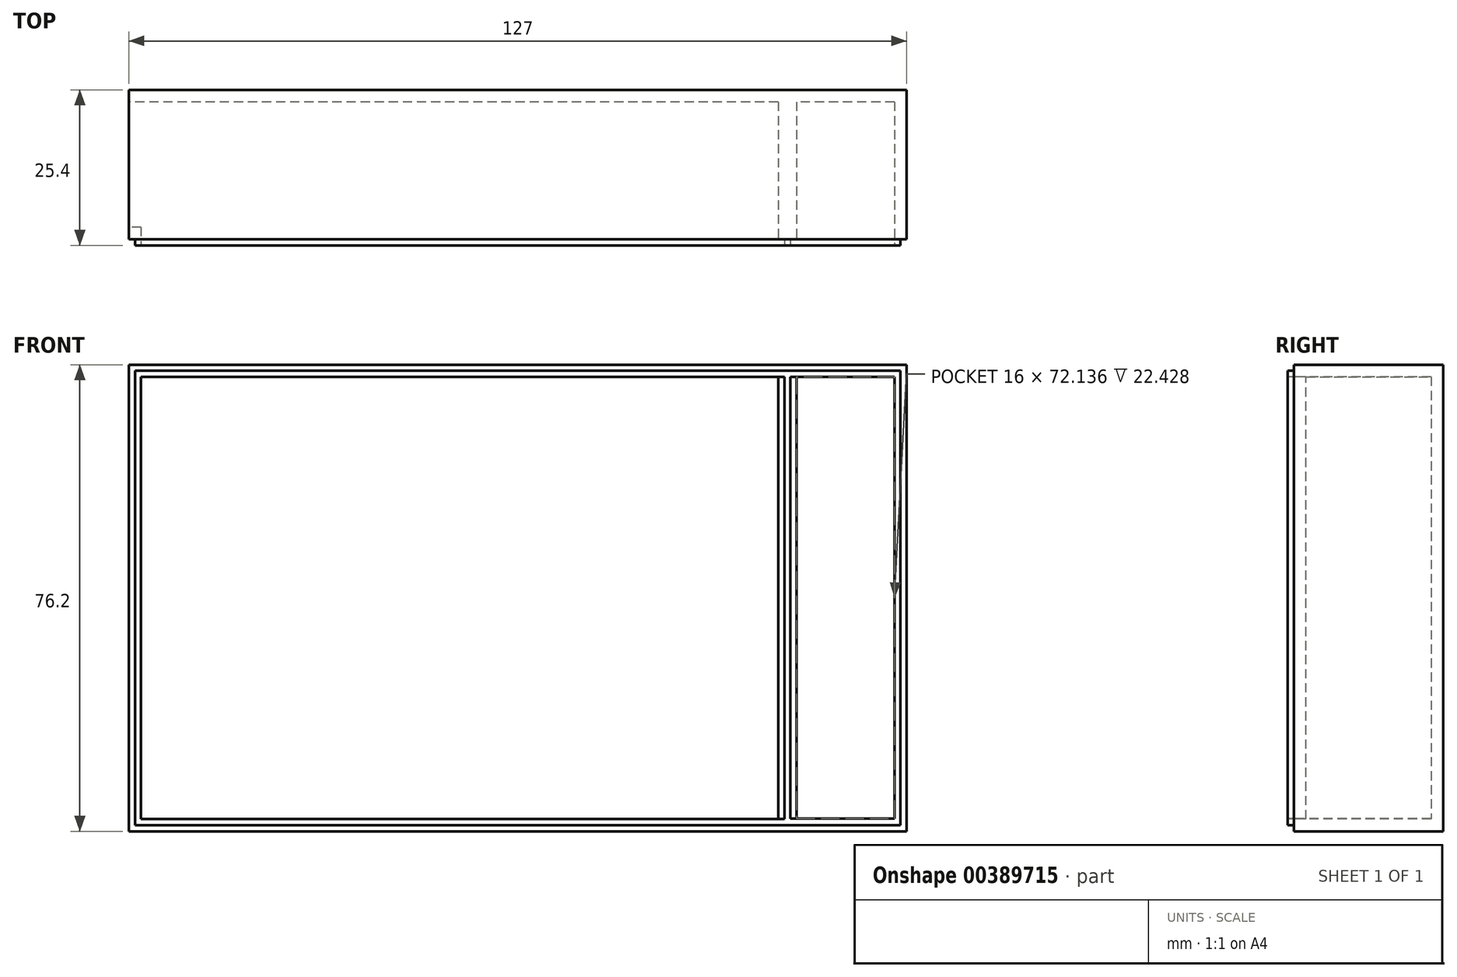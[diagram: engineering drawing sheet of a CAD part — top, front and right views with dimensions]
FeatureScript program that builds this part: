
annotation { "Feature Type Name" : "Feature", "Feature Type Description" : "" }
export const myFeature = defineFeature(function(context is Context, id is Id, definition is map)
    precondition{}
    {
        {
            var Q0;
            Q0=qCreatedBy(makeId("Front.planeOp"),FACE);
            var sketch = newSketch(context, id + "F0", { "sketchPlane" : qUnion([Q0])});
            skLineSegment(sketch, "E0.bottom", {"start": v(-63.5, 38.1) * mm, "end": v(63.5, 38.1) * mm});
            skLineSegment(sketch, "E0.top", {"start": v(-63.5, -38.1) * mm, "end": v(63.5, -38.1) * mm});
            skLineSegment(sketch, "E0.left", {"start": v(-63.5, 38.1) * mm, "end": v(-63.5, -38.1) * mm});
            skLineSegment(sketch, "E0.right", {"start": v(63.5, 38.1) * mm, "end": v(63.5, -38.1) * mm});
            skPoint(sketch, "E0.middle", {"position": v(0, 0) * mm});
            skSolve(sketch);
        }
        {
            var Q0;
            Q0=makeQuery(id+"F0.imprint","IMPRINT",FACE,{"disambiguationData":[TD([[makeQuery(id+"F0.imprint","IMPRINT",EDGE,{"derivedFrom":sQuery(id+"F0.wireOp",EDGE,"E0.bottom")}),-1.0]])]});
            extrude(context, id + "F1", {"entities" : qUnion([Q0]), "depth" : 25.4 * mm});
        }
        {
            var Q0;
            Q0=makeQuery(id+"F1.opExtrude","CAP_FACE",FACE,{"disambiguationData":[OSD([sQuery(id+"F0.wireOp",EDGE,"E0.bottom"),sQuery(id+"F0.wireOp",EDGE,"E0.top"),sQuery(id+"F0.wireOp",EDGE,"E0.left"),sQuery(id+"F0.wireOp",EDGE,"E0.right")])],"isStart":false});
            var sketch = newSketch(context, id + "F2", { "sketchPlane" : qUnion([Q0])});
            skLineSegment(sketch, "E1", {"start": v(45.52, 36.12) * mm, "end": v(45.52, -36.02) * mm});
            skLineSegment(sketch, "E2", {"start": v(45.52, -36.02) * mm, "end": v(61.52, -36.02) * mm});
            skLineSegment(sketch, "E3", {"start": v(61.52, -36.02) * mm, "end": v(61.52, 36.12) * mm});
            skLineSegment(sketch, "E4", {"start": v(61.52, 36.12) * mm, "end": v(45.52, 36.12) * mm});
            skSolve(sketch);
        }
        {
            var Q0;
            Q0=makeQuery(id+"F2.imprint","IMPRINT",FACE,{"disambiguationData":[TD([[makeQuery(id+"F2.imprint","IMPRINT",EDGE,{"derivedFrom":sQuery(id+"F2.wireOp",EDGE,"E1")}),1.0]])]});
            extrude(context, id + "F3", {"entities" : qUnion([Q0]), "operationType" : NewBodyOperationType.REMOVE, "oppositeDirection" : true, "depth" : 23.42 * mm});
        }
        {
            var Q0;
            Q0=makeQuery(id+"F1.opExtrude","CAP_FACE",FACE,{"disambiguationData":[OSD([sQuery(id+"F0.wireOp",EDGE,"E0.bottom"),sQuery(id+"F0.wireOp",EDGE,"E0.top"),sQuery(id+"F0.wireOp",EDGE,"E0.left"),sQuery(id+"F0.wireOp",EDGE,"E0.right")])],"isStart":false});
            var sketch = newSketch(context, id + "F4", { "sketchPlane" : qUnion([Q0])});
            skLineSegment(sketch, "E5.bottom", {"start": v(45.52, 36.12) * mm, "end": v(44.53, 36.12) * mm});
            skLineSegment(sketch, "E5.top", {"start": v(45.52, -36.02) * mm, "end": v(44.53, -36.02) * mm});
            skLineSegment(sketch, "E5.left", {"start": v(45.52, 36.12) * mm, "end": v(45.52, -36.02) * mm});
            skLineSegment(sketch, "E5.right", {"start": v(44.53, 36.12) * mm, "end": v(44.53, -36.02) * mm});
            skSolve(sketch);
        }
        {
            var Q0;
            Q0=makeQuery(id+"F4.imprint","IMPRINT",FACE,{"disambiguationData":[TD([[makeQuery(id+"F4.imprint","IMPRINT",EDGE,{"derivedFrom":sQuery(id+"F4.wireOp",EDGE,"E5.bottom")}),1.0]])]});
            extrude(context, id + "F5", {"entities" : qUnion([Q0]), "operationType" : NewBodyOperationType.REMOVE, "oppositeDirection" : true, "depth" : 1 * mm});
        }
        {
            var Q0;
            Q0=makeQuery(id+"F1.opExtrude","CAP_FACE",FACE,{"disambiguationData":[OSD([sQuery(id+"F0.wireOp",EDGE,"E0.bottom"),sQuery(id+"F0.wireOp",EDGE,"E0.top"),sQuery(id+"F0.wireOp",EDGE,"E0.left"),sQuery(id+"F0.wireOp",EDGE,"E0.right")])],"isStart":false});
            var sketch = newSketch(context, id + "F6", { "sketchPlane" : qUnion([Q0])});
            skLineSegment(sketch, "E6.bottom", {"start": v(-63.5, 38.1) * mm, "end": v(63.5, 38.1) * mm});
            skLineSegment(sketch, "E6.top", {"start": v(-63.5, 37.1) * mm, "end": v(63.5, 37.1) * mm});
            skLineSegment(sketch, "E6.left", {"start": v(-63.5, 38.1) * mm, "end": v(-63.5, 37.1) * mm});
            skLineSegment(sketch, "E6.right", {"start": v(63.5, 38.1) * mm, "end": v(63.5, 37.1) * mm});
            skSolve(sketch);
        }
        {
            var Q0;
            Q0=makeQuery(id+"F6.imprint","IMPRINT",FACE,{"disambiguationData":[TD([[makeQuery(id+"F6.imprint","IMPRINT",EDGE,{"derivedFrom":sQuery(id+"F6.wireOp",EDGE,"E6.bottom")}),-1.0]])]});
            extrude(context, id + "F7", {"entities" : qUnion([Q0]), "operationType" : NewBodyOperationType.REMOVE, "oppositeDirection" : true, "depth" : 1 * mm});
        }
        {
            var Q0;
            Q0=makeQuery(id+"F1.opExtrude","CAP_FACE",FACE,{"disambiguationData":[OSD([sQuery(id+"F0.wireOp",EDGE,"E0.bottom"),sQuery(id+"F0.wireOp",EDGE,"E0.top"),sQuery(id+"F0.wireOp",EDGE,"E0.left"),sQuery(id+"F0.wireOp",EDGE,"E0.right")])],"isStart":false});
            var sketch = newSketch(context, id + "F8", { "sketchPlane" : qUnion([Q0])});
            skLineSegment(sketch, "E7.bottom", {"start": v(63.5, 37.1) * mm, "end": v(62.5, 37.1) * mm});
            skLineSegment(sketch, "E7.top", {"start": v(63.5, -38.1) * mm, "end": v(62.5, -38.1) * mm});
            skLineSegment(sketch, "E7.left", {"start": v(63.5, 37.1) * mm, "end": v(63.5, -38.1) * mm});
            skLineSegment(sketch, "E7.right", {"start": v(62.5, 37.1) * mm, "end": v(62.5, -38.1) * mm});
            skSolve(sketch);
        }
        {
            var Q0;
            Q0=makeQuery(id+"F8.imprint","IMPRINT",FACE,{"disambiguationData":[TD([[makeQuery(id+"F8.imprint","IMPRINT",EDGE,{"derivedFrom":sQuery(id+"F8.wireOp",EDGE,"E7.bottom")}),-1.0]])]});
            extrude(context, id + "F9", {"entities" : qUnion([Q0]), "operationType" : NewBodyOperationType.REMOVE, "oppositeDirection" : true, "depth" : 1 * mm});
        }
        {
            var Q0;
            Q0=makeQuery(id+"F1.opExtrude","CAP_FACE",FACE,{"disambiguationData":[OSD([sQuery(id+"F0.wireOp",EDGE,"E0.bottom"),sQuery(id+"F0.wireOp",EDGE,"E0.top"),sQuery(id+"F0.wireOp",EDGE,"E0.left"),sQuery(id+"F0.wireOp",EDGE,"E0.right")])],"isStart":false});
            var sketch = newSketch(context, id + "F10", { "sketchPlane" : qUnion([Q0])});
            skLineSegment(sketch, "E8.bottom", {"start": v(-63.5, 37.1) * mm, "end": v(-62.5, 37.1) * mm});
            skLineSegment(sketch, "E8.top", {"start": v(-63.5, -38.1) * mm, "end": v(-62.5, -38.1) * mm});
            skLineSegment(sketch, "E8.left", {"start": v(-63.5, 37.1) * mm, "end": v(-63.5, -38.1) * mm});
            skLineSegment(sketch, "E8.right", {"start": v(-62.5, 37.1) * mm, "end": v(-62.5, -38.1) * mm});
            skSolve(sketch);
        }
        {
            var Q0;
            Q0=makeQuery(id+"F10.imprint","IMPRINT",FACE,{"disambiguationData":[TD([[makeQuery(id+"F10.imprint","IMPRINT",EDGE,{"derivedFrom":sQuery(id+"F10.wireOp",EDGE,"E8.bottom")}),-1.0]])]});
            extrude(context, id + "F11", {"entities" : qUnion([Q0]), "operationType" : NewBodyOperationType.REMOVE, "oppositeDirection" : true, "depth" : 1 * mm});
        }
        {
            var Q0;
            Q0=makeQuery(id+"F1.opExtrude","CAP_FACE",FACE,{"disambiguationData":[OSD([sQuery(id+"F0.wireOp",EDGE,"E0.bottom"),sQuery(id+"F0.wireOp",EDGE,"E0.top"),sQuery(id+"F0.wireOp",EDGE,"E0.left"),sQuery(id+"F0.wireOp",EDGE,"E0.right")])],"isStart":false});
            var sketch = newSketch(context, id + "F12", { "sketchPlane" : qUnion([Q0])});
            skLineSegment(sketch, "E9.bottom", {"start": v(-62.5, -38.1) * mm, "end": v(62.5, -38.1) * mm});
            skLineSegment(sketch, "E9.top", {"start": v(-62.5, -37.1) * mm, "end": v(62.5, -37.1) * mm});
            skLineSegment(sketch, "E9.left", {"start": v(-62.5, -38.1) * mm, "end": v(-62.5, -37.1) * mm});
            skLineSegment(sketch, "E9.right", {"start": v(62.5, -38.1) * mm, "end": v(62.5, -37.1) * mm});
            skSolve(sketch);
        }
        {
            var Q0;
            Q0=makeQuery(id+"F12.imprint","IMPRINT",FACE,{"disambiguationData":[TD([[makeQuery(id+"F12.imprint","IMPRINT",EDGE,{"derivedFrom":sQuery(id+"F12.wireOp",EDGE,"E9.bottom")}),1.0]])]});
            extrude(context, id + "F13", {"entities" : qUnion([Q0]), "operationType" : NewBodyOperationType.REMOVE, "oppositeDirection" : true, "depth" : 1 * mm});
        }
        {
            var Q0;
            Q0=makeQuery(id+"F1.opExtrude","CAP_FACE",FACE,{"disambiguationData":[OSD([sQuery(id+"F0.wireOp",EDGE,"E0.bottom"),sQuery(id+"F0.wireOp",EDGE,"E0.top"),sQuery(id+"F0.wireOp",EDGE,"E0.left"),sQuery(id+"F0.wireOp",EDGE,"E0.right")])],"isStart":false});
            var sketch = newSketch(context, id + "F14", { "sketchPlane" : qUnion([Q0])});
            skLineSegment(sketch, "E10", {"start": v(-61.52, 36.12) * mm, "end": v(-61.52, -36.12) * mm});
            skLineSegment(sketch, "E11", {"start": v(-61.52, -36.12) * mm, "end": v(42.55, -36.12) * mm});
            skLineSegment(sketch, "E12", {"start": v(42.55, -36.12) * mm, "end": v(42.55, 36.12) * mm});
            skLineSegment(sketch, "E13", {"start": v(42.55, 36.12) * mm, "end": v(-61.52, 36.12) * mm});
            skSolve(sketch);
        }
        {
            var Q0;
            Q0=makeQuery(id+"F14.imprint","IMPRINT",FACE,{"disambiguationData":[TD([[makeQuery(id+"F14.imprint","IMPRINT",EDGE,{"derivedFrom":sQuery(id+"F14.wireOp",EDGE,"E10")}),1.0]])]});
            extrude(context, id + "F15", {"entities" : qUnion([Q0]), "operationType" : NewBodyOperationType.REMOVE, "oppositeDirection" : true, "depth" : 23.42 * mm});
        }
        {
            var Q0;
            Q0=makeQuery(id+"F1.opExtrude","CAP_FACE",FACE,{"disambiguationData":[OSD([sQuery(id+"F0.wireOp",EDGE,"E0.bottom"),sQuery(id+"F0.wireOp",EDGE,"E0.top"),sQuery(id+"F0.wireOp",EDGE,"E0.left"),sQuery(id+"F0.wireOp",EDGE,"E0.right")])],"isStart":false});
            var sketch = newSketch(context, id + "F16", { "sketchPlane" : qUnion([Q0])});
            skLineSegment(sketch, "E14.bottom", {"start": v(42.55, 36.12) * mm, "end": v(43.54, 36.12) * mm});
            skLineSegment(sketch, "E14.top", {"start": v(42.55, -36.12) * mm, "end": v(43.54, -36.12) * mm});
            skLineSegment(sketch, "E14.left", {"start": v(42.55, 36.12) * mm, "end": v(42.55, -36.12) * mm});
            skLineSegment(sketch, "E14.right", {"start": v(43.54, 36.12) * mm, "end": v(43.54, -36.12) * mm});
            skSolve(sketch);
        }
        {
            var Q0;
            Q0 = qSketchRegion(id + "F16", true);
            extrude(context, id + "F17", {"entities" : qUnion([Q0]), "operationType" : NewBodyOperationType.REMOVE, "oppositeDirection" : true, "depth" : 1 * mm});
        }
        {
            var Q0;
            Q0=makeQuery(id+"F1.opExtrude","SWEPT_FACE",FACE,{"disambiguationData":[OSD([sQuery(id+"F0.wireOp",EDGE,"E0.left")])]});
            var sketch = newSketch(context, id + "F18", { "sketchPlane" : qUnion([Q0])});
            skLineSegment(sketch, "E15", {"start": v(22.43, 36.12) * mm, "end": v(1.98, 36.12) * mm});
            skLineSegment(sketch, "E16", {"start": v(1.98, 36.12) * mm, "end": v(1.98, -36.12) * mm});
            skLineSegment(sketch, "E17", {"start": v(1.98, -36.12) * mm, "end": v(22.43, -36.12) * mm});
            skLineSegment(sketch, "E18", {"start": v(22.43, -36.12) * mm, "end": v(22.43, 36.12) * mm});
            skSolve(sketch);
        }
        {
            var Q0;
            Q0=makeQuery(id+"F18.imprint","IMPRINT",FACE,{"disambiguationData":[TD([[makeQuery(id+"F18.imprint","IMPRINT",EDGE,{"derivedFrom":sQuery(id+"F18.wireOp",EDGE,"E15")}),1.0]])]});
            extrude(context, id + "F19", {"entities" : qUnion([Q0]), "operationType" : NewBodyOperationType.REMOVE, "oppositeDirection" : true, "depth" : 1.98 * mm});
        }
    });
